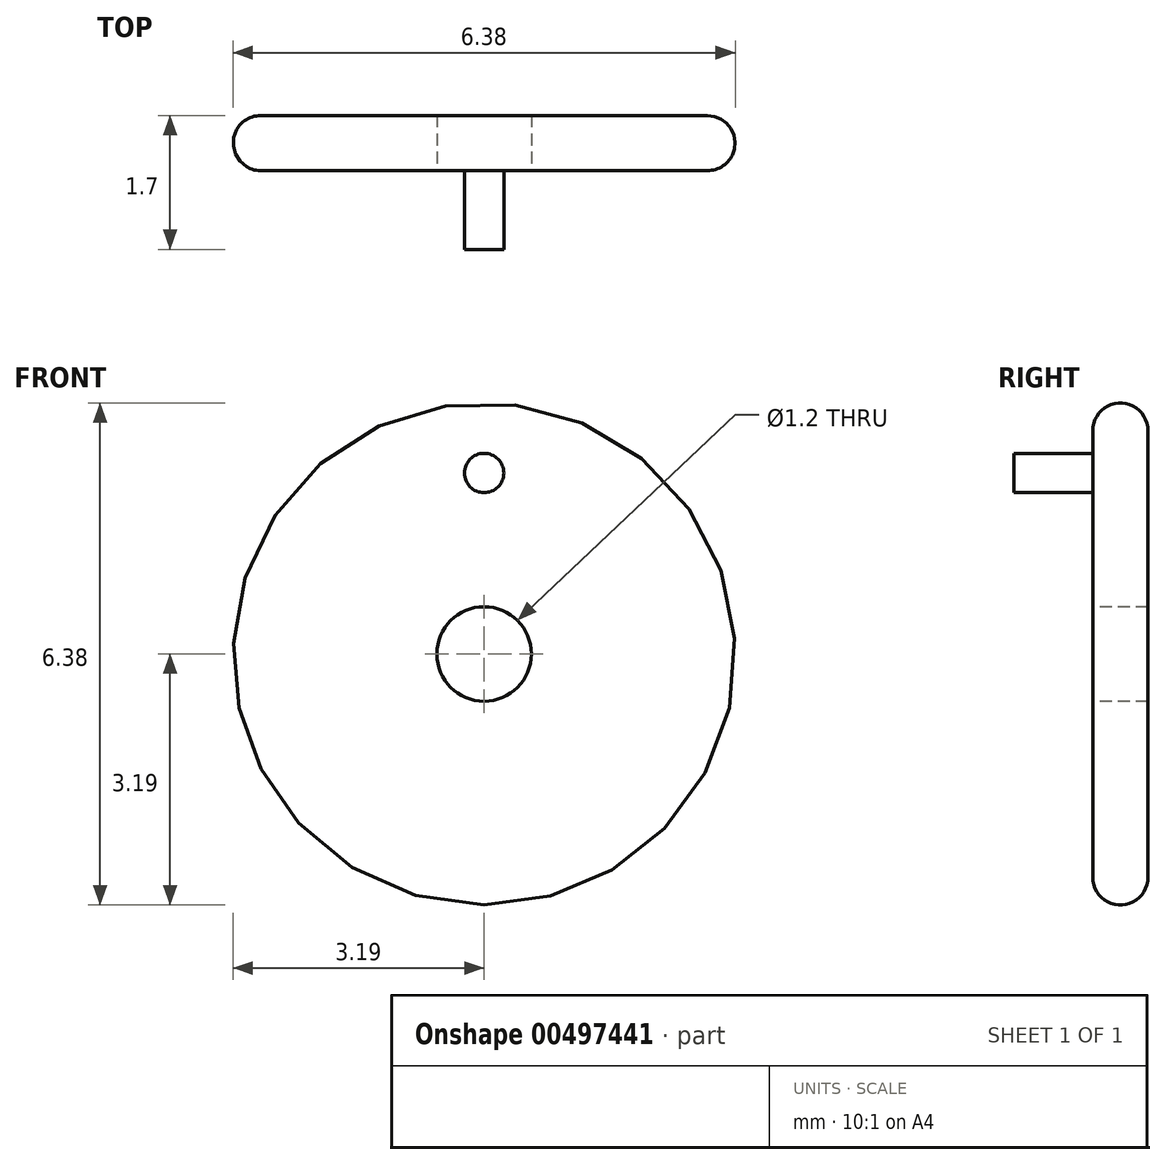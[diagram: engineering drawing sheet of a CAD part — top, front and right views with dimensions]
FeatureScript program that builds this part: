
annotation { "Feature Type Name" : "Feature", "Feature Type Description" : "" }
export const myFeature = defineFeature(function(context is Context, id is Id, definition is map)
    precondition{}
    {
        {
            var Q0;
            Q0=qCreatedBy(makeId("Front.planeOp"),FACE);
            var sketch = newSketch(context, id + "F0", { "sketchPlane" : qUnion([Q0])});
            skCircle(sketch, "E0", {"center": v(0, 0) * mm, "radius": 3.19 * mm});
            skSolve(sketch);
        }
        {
            var Q0;
            Q0 = qSketchRegion(id + "F0", true);
            extrude(context, id + "F1", {"entities" : qUnion([Q0]), "depth" : .7 * mm});
        }
        {
            var Q0;
            Q0=makeQuery(id+"F1.opExtrude","CAP_FACE",FACE,{"disambiguationData":[OSD([sQuery(id+"F0.wireOp",EDGE,"E0")])],"isStart":false});
            var sketch = newSketch(context, id + "F2", { "sketchPlane" : qUnion([Q0])});
            skCircle(sketch, "E1", {"center": v(0, 0) * mm, "radius": 0.6 * mm});
            skSolve(sketch);
        }
        {
            var Q0;
            Q0=makeQuery(id+"F2.imprint","IMPRINT",FACE,{"disambiguationData":[TD([[makeQuery(id+"F2.imprint","IMPRINT",EDGE,{"derivedFrom":sQuery(id+"F2.wireOp",EDGE,"E1")}),1.0]])]});
            extrude(context, id + "F3", {"entities" : qUnion([Q0]), "operationType" : NewBodyOperationType.REMOVE, "oppositeDirection" : true, "depth" : 25 * mm});
        }
        {
            var Q0;
            Q0=makeQuery(id+"F1.opExtrude","SWEPT_FACE",FACE,{"disambiguationData":[OSD([sQuery(id+"F0.wireOp",EDGE,"E0")])]});
            fillet(context, id + "F4", {"entities" : qUnion([Q0]), "radius" : .35 * mm, "tangentPropagation" : true, "allowEdgeOverflow" : false});
        }
        {
            var Q0;
            Q0=makeQuery(id+"F1.opExtrude","CAP_FACE",FACE,{"disambiguationData":[OSD([sQuery(id+"F0.wireOp",EDGE,"E0")])],"isStart":false});
            var sketch = newSketch(context, id + "F5", { "sketchPlane" : qUnion([Q0])});
            skCircle(sketch, "E2", {"center": v(0, 2.3) * mm, "radius": 0.25 * mm});
            skSolve(sketch);
        }
        {
            var Q0;
            Q0 = qSketchRegion(id + "F5", true);
            extrude(context, id + "F6", {"entities" : qUnion([Q0]), "operationType" : NewBodyOperationType.ADD, "depth" : 1 * mm});
        }
    });
